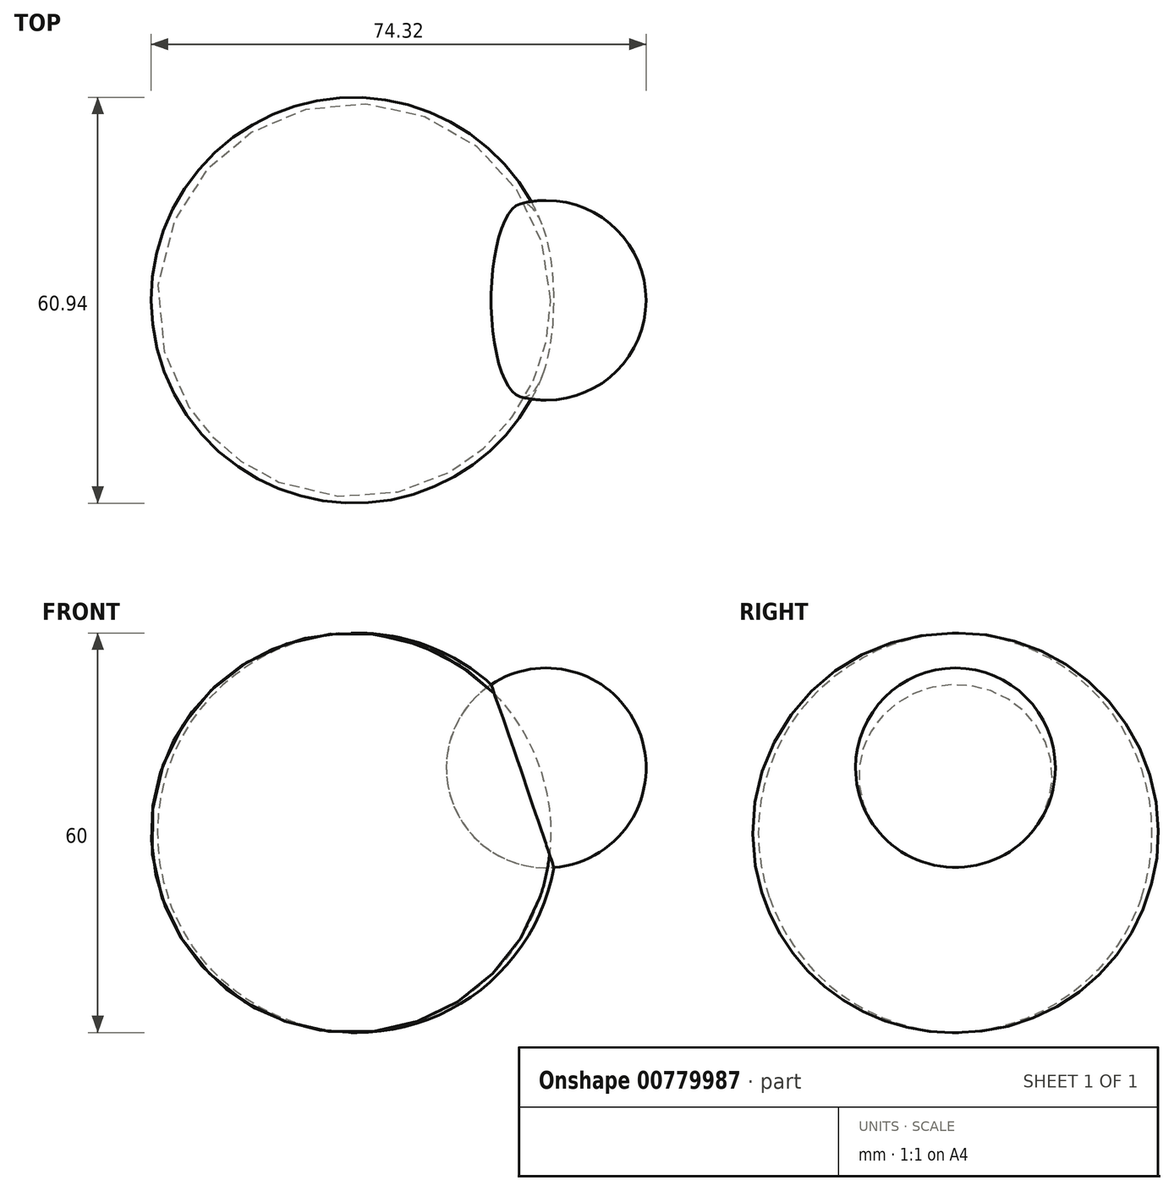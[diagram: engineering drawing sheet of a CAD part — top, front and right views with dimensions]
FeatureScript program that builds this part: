
annotation { "Feature Type Name" : "Feature", "Feature Type Description" : "" }
export const myFeature = defineFeature(function(context is Context, id is Id, definition is map)
    precondition{}
    {
        {
            var Q0;
            Q0=qCreatedBy(makeId("Front.planeOp"),FACE);
            var sketch = newSketch(context, id + "F0", { "sketchPlane" : qUnion([Q0])});
            skLineSegment(sketch, "E0", {"start": v(0, 0) * mm, "end": v(0, 60) * mm});
            skArc(sketch, "E1", {"start": v(0, 0) * mm, "mid": v(30.47, 30) * mm, "end": v(0, 60) * mm});
            skSolve(sketch);
        }
        {
            var Q0;
            {var subQ0=sQuery(id+"F0.wireOp",EDGE,"E1");Q0=makeQuery(id+"F0.imprint","IMPRINT",FACE,{"disambiguationData":[TD([[makeQuery(id+"F0.imprint","IMPRINT",EDGE,{"derivedFrom":subQ0}),1.0]])]});}
            var sketch = newSketch(context, id + "F1", { "sketchPlane" : qUnion([Q0])});
            skLineSegment(sketch, "E2", {"start": v(0, 59.63) * mm, "end": v(0, 0) * mm, "construction": true});
            skLineSegment(sketch, "E3", {"start": v(0, 29.81) * mm, "end": v(28.85, 39.75) * mm, "construction": true});
            skSolve(sketch);
        }
        {
            var Q0;
            {var subQ0=sQuery(id+"F0.wireOp",EDGE,"E1");Q0=makeQuery(id+"F1.imprint","IMPRINT",FACE,{"disambiguationData":[TD([[makeQuery(id+"F1.imprint","IMPRINT",EDGE,{"derivedFrom":makeQuery(id+"F0.imprint","IMPRINT",EDGE,{"derivedFrom":subQ0})}),1.0]])]});}
            var Q1;
            Q1=sQuery(id+"F1.wireOp",EDGE,"E2");
            revolve(context, id + "F2", {"surfaceOperationType" : NewSurfaceOperationType.NEW, "entities" : qUnion([Q0]), "axis" : qUnion([Q1]), "revolveType" : RevolveType.FULL});
        }
        {
            var Q0;
            Q0=sQuery(id+"F1.wireOp",VERTEX,"E3.end");
            var Q1;
            Q1=sQuery(id+"F1.wireOp",EDGE,"E3");
            cPlane(context, id + "F3", {"entities" : qUnion([Q0, Q1]), "cplaneType" : CPlaneType.LINE_POINT, "offset" : 25 * mm, "width" : 150 * mm, "height" : 150 * mm});
        }
        {
            var Q0;
            Q0=qCreatedBy(id+"F3.planeOp",FACE);
            var sketch = newSketch(context, id + "F4", { "sketchPlane" : qUnion([Q0])});
            skLineSegment(sketch, "E4", {"start": v(15, 28.2) * mm, "end": v(-15, 28.2) * mm});
            skArc(sketch, "E5", {"start": v(-15, 28.2) * mm, "mid": v(0, 13.2) * mm, "end": v(15, 28.2) * mm});
            skSolve(sketch);
        }
        {
            var Q0;
            Q0=makeQuery(id+"F4.imprint","IMPRINT",FACE,{"disambiguationData":[TD([[makeQuery(id+"F4.imprint","IMPRINT",EDGE,{"derivedFrom":sQuery(id+"F4.wireOp",EDGE,"E4")}),1.0]])]});
            var Q1;
            Q1=sQuery(id+"F4.wireOp",EDGE,"E4");
            revolve(context, id + "F5", {"operationType" : NewBodyOperationType.ADD, "surfaceOperationType" : NewSurfaceOperationType.NEW, "entities" : qUnion([Q0]), "axis" : qUnion([Q1]), "revolveType" : RevolveType.FULL});
        }
        {
            var Q0;
            Q0=sQuery(id+"F0.wireOp",VERTEX,"E1.start");
            var Q1;
            Q1=sQuery(id+"F1.wireOp",EDGE,"E2");
            cPlane(context, id + "F6", {"entities" : qUnion([Q0, Q1]), "cplaneType" : CPlaneType.LINE_POINT, "offset" : 25 * mm, "width" : 150 * mm, "height" : 150 * mm});
        }
        {
            var Q0;
            Q0=qCreatedBy(id+"F6.planeOp",FACE);
            var sketch = newSketch(context, id + "F7", { "sketchPlane" : qUnion([Q0])});
            skLineSegment(sketch, "E6", {"start": v(-15, 0.04) * mm, "end": v(15, 0.04) * mm});
            skArc(sketch, "E7", {"start": v(15, 0.04) * mm, "mid": v(0, 15) * mm, "end": v(-15, 0.04) * mm});
            skSolve(sketch);
        }
        {
            var Q0;
            Q0=sQuery(id+"F7.wireOp",EDGE,"E7");
            var Q1;
            Q1=sQuery(id+"F7.wireOp",EDGE,"E6");
            revolve(context, id + "F8", {"bodyType" : ToolBodyType.SURFACE, "surfaceOperationType" : NewSurfaceOperationType.NEW, "surfaceEntities" : qUnion([Q0]), "axis" : qUnion([Q1]), "revolveType" : RevolveType.FULL});
        }
    });
